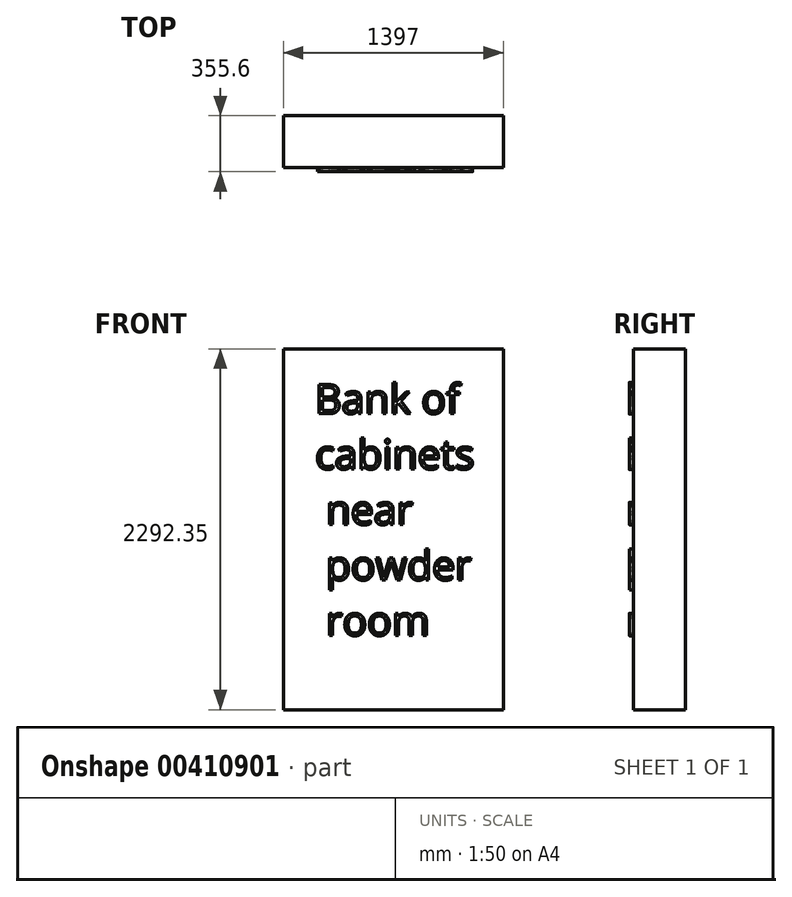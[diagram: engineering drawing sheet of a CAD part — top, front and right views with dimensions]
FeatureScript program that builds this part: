
annotation { "Feature Type Name" : "Feature", "Feature Type Description" : "" }
export const myFeature = defineFeature(function(context is Context, id is Id, definition is map)
    precondition{}
    {
        {
            var Q0;
            Q0=qCreatedBy(makeId("Front.planeOp"),FACE);
            var sketch = newSketch(context, id + "F0", { "sketchPlane" : qUnion([Q0])});
            skLineSegment(sketch, "E0.bottom", {"start": v(-1331.12, 2261.84) * mm, "end": v(65.88, 2261.84) * mm});
            skLineSegment(sketch, "E0.top", {"start": v(-1331.12, -30.5) * mm, "end": v(65.88, -30.5) * mm});
            skLineSegment(sketch, "E0.left", {"start": v(-1331.12, 2261.84) * mm, "end": v(-1331.12, -30.5) * mm});
            skLineSegment(sketch, "E0.right", {"start": v(65.88, 2261.84) * mm, "end": v(65.88, -30.5) * mm});
            skSolve(sketch);
        }
        {
            var Q0;
            Q0 = qSketchRegion(id + "F0", true);
            extrude(context, id + "F1", {"entities" : qUnion([Q0]), "depth" : 330.2 * mm});
        }
        {
            var Q0;
            Q0=makeQuery(id+"F1.opExtrude","CAP_FACE",FACE,{"disambiguationData":[OSD([sQuery(id+"F0.wireOp",EDGE,"E0.bottom"),sQuery(id+"F0.wireOp",EDGE,"E0.top"),sQuery(id+"F0.wireOp",EDGE,"E0.left"),sQuery(id+"F0.wireOp",EDGE,"E0.right")])],"isStart":false});
            var sketch = newSketch(context, id + "F2", { "sketchPlane" : qUnion([Q0])});
            skText(sketch, "E1", { "text": "Bank of \ncabinets\n near\n powder\n room", "fontName": "OpenSans-Regular.ttf"});
            const initialGuessF2  = {"E1": [-1.12893, 1.8505, 1, 0, 0.18653]};
            skSetInitialGuess(sketch, initialGuessF2);
            skSolve(sketch);
        }
        {
            var Q0;
            Q0 = qSketchRegion(id + "F2", true);
            extrude(context, id + "F3", {"entities" : qUnion([Q0]), "operationType" : NewBodyOperationType.ADD, "depth" : 25.4 * mm});
        }
    });
